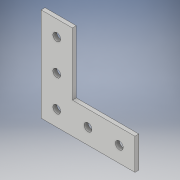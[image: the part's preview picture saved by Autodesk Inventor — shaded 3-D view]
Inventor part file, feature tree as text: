
AUTODESK INVENTOR PART (.ipt)
format: ipt  version: 2018 (Build 220112000, 112)  size: 106,496 bytes
history: native  units: in
note: dims shown in document units (in); Inventor stores cm internally (conversion verified against a paired STEP export)
features: hole x5
ambient origin geometry x8: Origin, YZ Plane, XZ Plane, XY Plane, X Axis, Y Axis, Z Axis, Center Point
bodies: Solid1 (feature_tree), Body1 (feature_tree)
feature tree (5):
  hole  "Hole1"  [1 undecoded]
  hole  "Hole2"  [1 undecoded]
  hole  "Hole3"  [1 undecoded]
  hole  "Hole4"  [1 undecoded]
  hole  "Hole5"  [1 undecoded]
note: 5 required parameter values undecoded (feature->parameter linkage not recoverable at this tier; creation-order binding heuristic only, values carry confidence <= 0.55)
